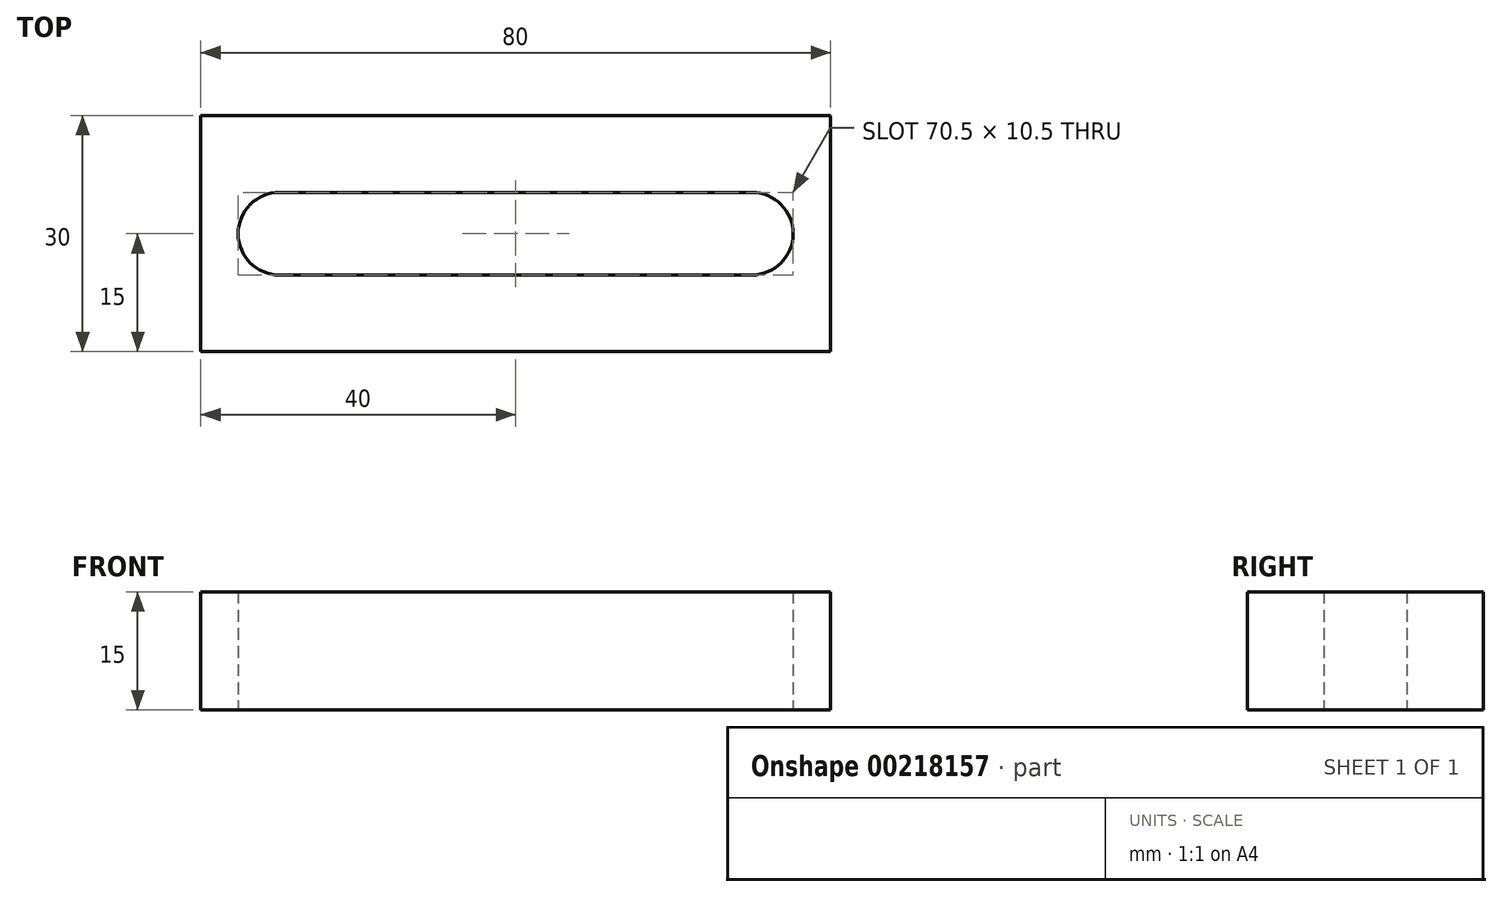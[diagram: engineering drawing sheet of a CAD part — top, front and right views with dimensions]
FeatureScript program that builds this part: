
annotation { "Feature Type Name" : "Feature", "Feature Type Description" : "" }
export const myFeature = defineFeature(function(context is Context, id is Id, definition is map)
    precondition{}
    {
        {
            var Q0;
            Q0=qCreatedBy(makeId("Top.planeOp"),FACE);
            var sketch = newSketch(context, id + "F0", { "sketchPlane" : qUnion([Q0])});
            skLineSegment(sketch, "E0.bottom", {"start": v(-40, 15) * mm, "end": v(40, 15) * mm});
            skLineSegment(sketch, "E0.top", {"start": v(-40, -15) * mm, "end": v(40, -15) * mm});
            skLineSegment(sketch, "E0.left", {"start": v(-40, 15) * mm, "end": v(-40, -15) * mm});
            skLineSegment(sketch, "E0.right", {"start": v(40, 15) * mm, "end": v(40, -15) * mm});
            skLineSegment(sketch, "E1", {"start": v(-30, 0) * mm, "end": v(30, 0) * mm, "construction": true});
            skArc(sketch, "E2.0.startCap", {"start": v(-30, -5.25) * mm, "mid": v(-35.25, 0) * mm, "end": v(-30, 5.25) * mm});
            skArc(sketch, "E2.0.endCap", {"start": v(30, 5.25) * mm, "mid": v(35.25, 0) * mm, "end": v(30, -5.25) * mm});
            skLineSegment(sketch, "E2.0.left", {"start": v(-30, 5.25) * mm, "end": v(30, 5.25) * mm});
            skLineSegment(sketch, "E2.0.right", {"start": v(-30, -5.25) * mm, "end": v(30, -5.25) * mm});
            skSolve(sketch);
        }
        {
            var Q0;
            Q0 = qSketchRegion(id + "F0", true);
            extrude(context, id + "F1", {"entities" : qUnion([Q0]), "depth" : 15 * mm, "offsetDistance" : 25 * mm});
        }
    });
